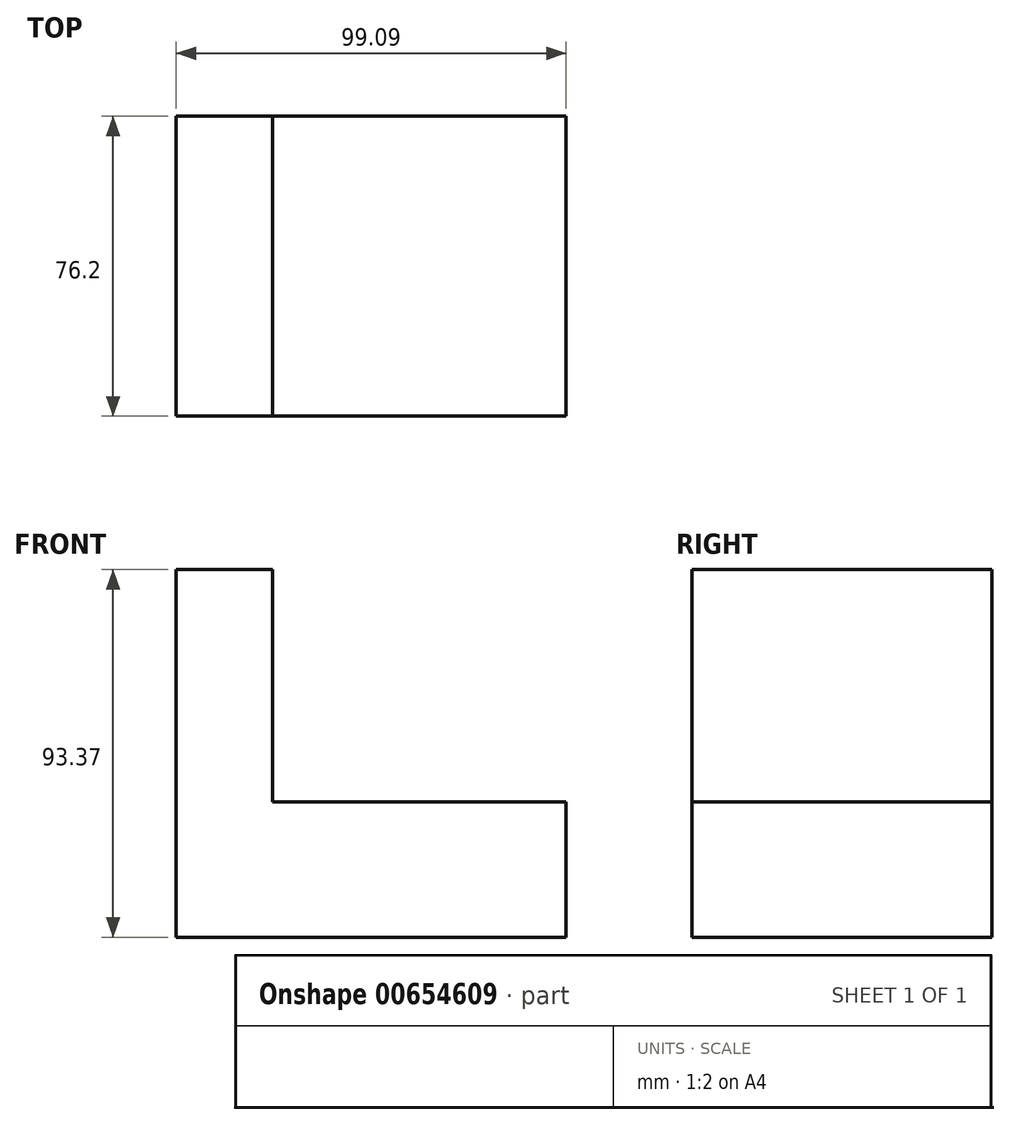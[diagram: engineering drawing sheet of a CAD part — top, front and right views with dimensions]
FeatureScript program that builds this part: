
annotation { "Feature Type Name" : "Feature", "Feature Type Description" : "" }
export const myFeature = defineFeature(function(context is Context, id is Id, definition is map)
    precondition{}
    {
        {
            var Q0;
            Q0=qCreatedBy(makeId("Front.planeOp"),FACE);
            var sketch = newSketch(context, id + "F0", { "sketchPlane" : qUnion([Q0])});
            skLineSegment(sketch, "E0", {"start": v(-51.63, -56.6) * mm, "end": v(41.4, -56.6) * mm});
            skLineSegment(sketch, "E1", {"start": v(41.4, -56.6) * mm, "end": v(41.4, -22.17) * mm});
            skLineSegment(sketch, "E2", {"start": v(41.4, -22.17) * mm, "end": v(-33.19, -22.17) * mm});
            skLineSegment(sketch, "E3", {"start": v(-33.19, 36.77) * mm, "end": v(-33.19, -22.17) * mm});
            skLineSegment(sketch, "E4", {"start": v(-57.7, 36.77) * mm, "end": v(-33.19, 36.77) * mm});
            skLineSegment(sketch, "E5", {"start": v(-57.7, 36.77) * mm, "end": v(-57.7, -56.6) * mm});
            skLineSegment(sketch, "E6", {"start": v(-57.7, -56.6) * mm, "end": v(-51.63, -56.6) * mm});
            skSolve(sketch);
        }
        {
            var Q0;
            Q0=makeQuery(id+"F0.imprint","IMPRINT",FACE,{"disambiguationData":[TD([[makeQuery(id+"F0.imprint","IMPRINT",EDGE,{"derivedFrom":sQuery(id+"F0.wireOp",EDGE,"E0")}),1.0]])]});
            extrude(context, id + "F1", {"entities" : qUnion([Q0]), "depth" : 76.2 * mm, "offsetDistance" : 25.4 * mm});
        }
    });
